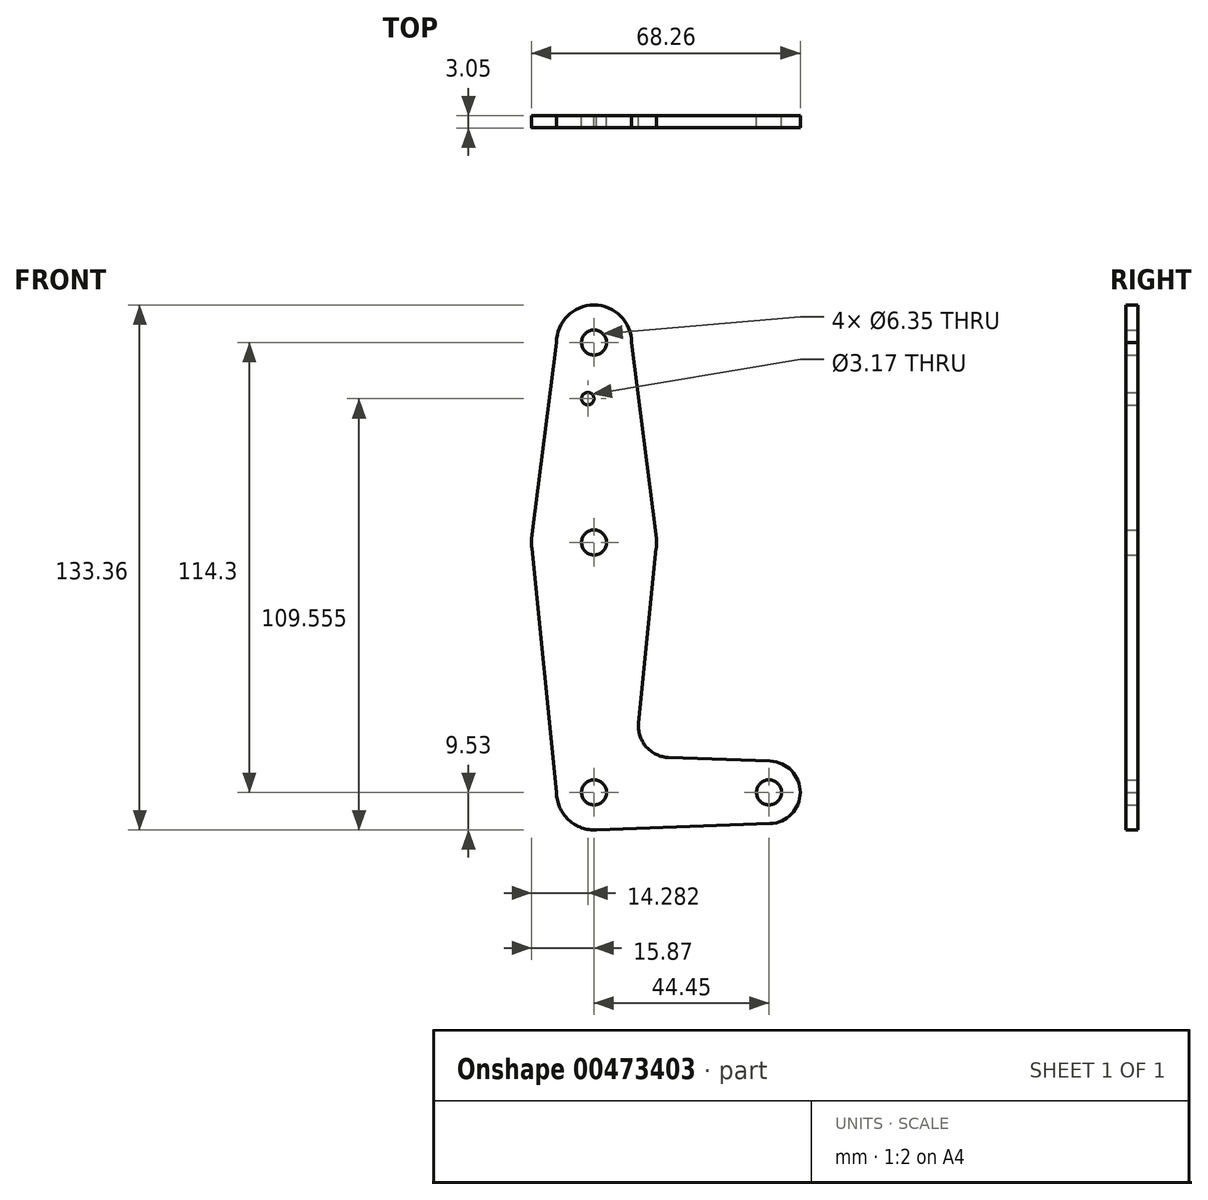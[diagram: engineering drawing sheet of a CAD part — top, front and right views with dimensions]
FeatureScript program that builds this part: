
annotation { "Feature Type Name" : "Feature", "Feature Type Description" : "" }
export const myFeature = defineFeature(function(context is Context, id is Id, definition is map)
    precondition{}
    {
        {
            var Q0;
            Q0=qCreatedBy(makeId("Front.planeOp"),FACE);
            var sketch = newSketch(context, id + "F0", { "sketchPlane" : qUnion([Q0])});
            skLineSegment(sketch, "E0", {"start": v(0, 114.3) * mm, "end": v(0, 0) * mm, "construction": true});
            skCircle(sketch, "E1", {"center": v(0, 114.3) * mm, "radius": 9.53 * mm});
            skCircle(sketch, "E2", {"center": v(0, 63.5) * mm, "radius": 15.88 * mm});
            skCircle(sketch, "E3", {"center": v(0, 0) * mm, "radius": 9.53 * mm});
            skLineSegment(sketch, "E4", {"start": v(0, 0) * mm, "end": v(44.45, 0) * mm, "construction": true});
            skCircle(sketch, "E5", {"center": v(44.45, 0) * mm, "radius": 7.94 * mm});
            skLineSegment(sketch, "E6", {"start": v(-9.52, 0) * mm, "end": v(-15.8, 61.9) * mm});
            skLineSegment(sketch, "E7", {"start": v(9.52, 114.3) * mm, "end": v(15.75, 65.5) * mm});
            skLineSegment(sketch, "E8", {"start": v(-9.53, 114.3) * mm, "end": v(-15.75, 65.5) * mm});
            skLineSegment(sketch, "E9", {"start": v(0, -9.53) * mm, "end": v(44.73, -7.93) * mm});
            skCircle(sketch, "E10", {"center": v(0, 114.3) * mm, "radius": 3.18 * mm});
            skCircle(sketch, "E11", {"center": v(0, 63.5) * mm, "radius": 3.18 * mm});
            skCircle(sketch, "E12", {"center": v(0, 0) * mm, "radius": 3.18 * mm});
            skCircle(sketch, "E13", {"center": v(44.45, 0) * mm, "radius": 3.18 * mm});
            skCircle(sketch, "E14", {"center": v(-1.59, 100.03) * mm, "radius": 1.59 * mm});
            skPoint(sketch, "E14.centerSnap0", {"position": v(-12.64, 89.9) * mm});
            skLineSegment(sketch, "E15", {"start": v(11.34, 17.6) * mm, "end": v(15.8, 61.91) * mm});
            skLineSegment(sketch, "E16", {"start": v(18.97, 8.85) * mm, "end": v(44.73, 7.93) * mm});
            skArc(sketch, "E17.filletArc", {"start": v(11.34, 17.6) * mm, "mid": v(13.26, 11.57) * mm, "end": v(18.97, 8.85) * mm});
            skSolve(sketch);
        }
        {
            var Q0;
            Q0 = qSketchRegion(id + "F0", true);
            extrude(context, id + "F1", {"entities" : qUnion([Q0]), "depth" : 3.05 * mm});
        }
    });
